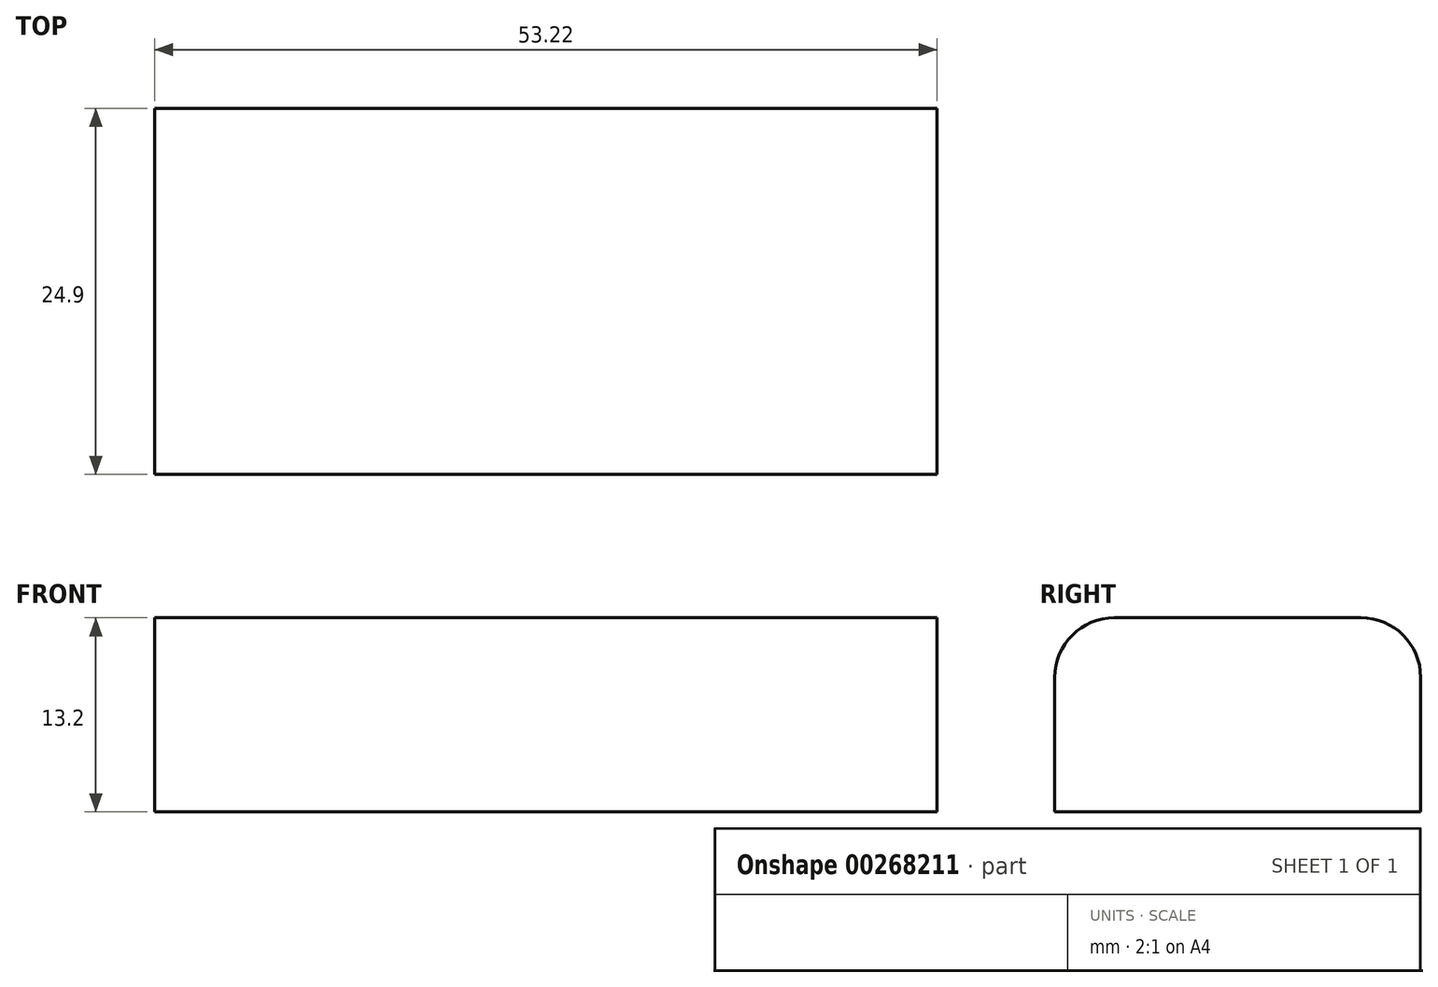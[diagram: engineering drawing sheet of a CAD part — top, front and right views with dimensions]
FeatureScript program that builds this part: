
annotation { "Feature Type Name" : "Feature", "Feature Type Description" : "" }
export const myFeature = defineFeature(function(context is Context, id is Id, definition is map)
    precondition{}
    {
        {
            var Q0;
            Q0=qCreatedBy(makeId("Right.planeOp"),FACE);
            var sketch = newSketch(context, id + "F0", { "sketchPlane" : qUnion([Q0])});
            skLineSegment(sketch, "E0.bottom", {"start": v(8.38, 6.6) * mm, "end": v(-8.38, 6.6) * mm});
            skLineSegment(sketch, "E0.top", {"start": v(12.45, -6.6) * mm, "end": v(-12.45, -6.6) * mm});
            skLineSegment(sketch, "E0.left", {"start": v(12.45, 2.54) * mm, "end": v(12.45, -6.6) * mm});
            skLineSegment(sketch, "E0.right", {"start": v(-12.45, 2.54) * mm, "end": v(-12.45, -6.6) * mm});
            skPoint(sketch, "E0.middle", {"position": v(0, 0) * mm});
            skPoint(sketch, "E1.visualSharp", {"position": v(-12.45, 6.6) * mm});
            skArc(sketch, "E1.filletArc", {"start": v(-8.38, 6.6) * mm, "mid": v(-11.26, 5.41) * mm, "end": v(-12.45, 2.54) * mm});
            skPoint(sketch, "E2.visualSharp", {"position": v(12.45, 6.6) * mm});
            skArc(sketch, "E2.filletArc", {"start": v(12.45, 2.54) * mm, "mid": v(11.26, 5.41) * mm, "end": v(8.38, 6.6) * mm});
            skSolve(sketch);
        }
        {
            var Q0;
            Q0=makeQuery(id+"F0.imprint","IMPRINT",FACE,{"disambiguationData":[TD([[makeQuery(id+"F0.imprint","IMPRINT",EDGE,{"derivedFrom":sQuery(id+"F0.wireOp",EDGE,"E0.bottom")}),1.0]])]});
            extrude(context, id + "F1", {"entities" : qUnion([Q0]), "endBound" : BoundingType.SYMMETRIC, "depth" : 53.2 * mm});
        }
    });
